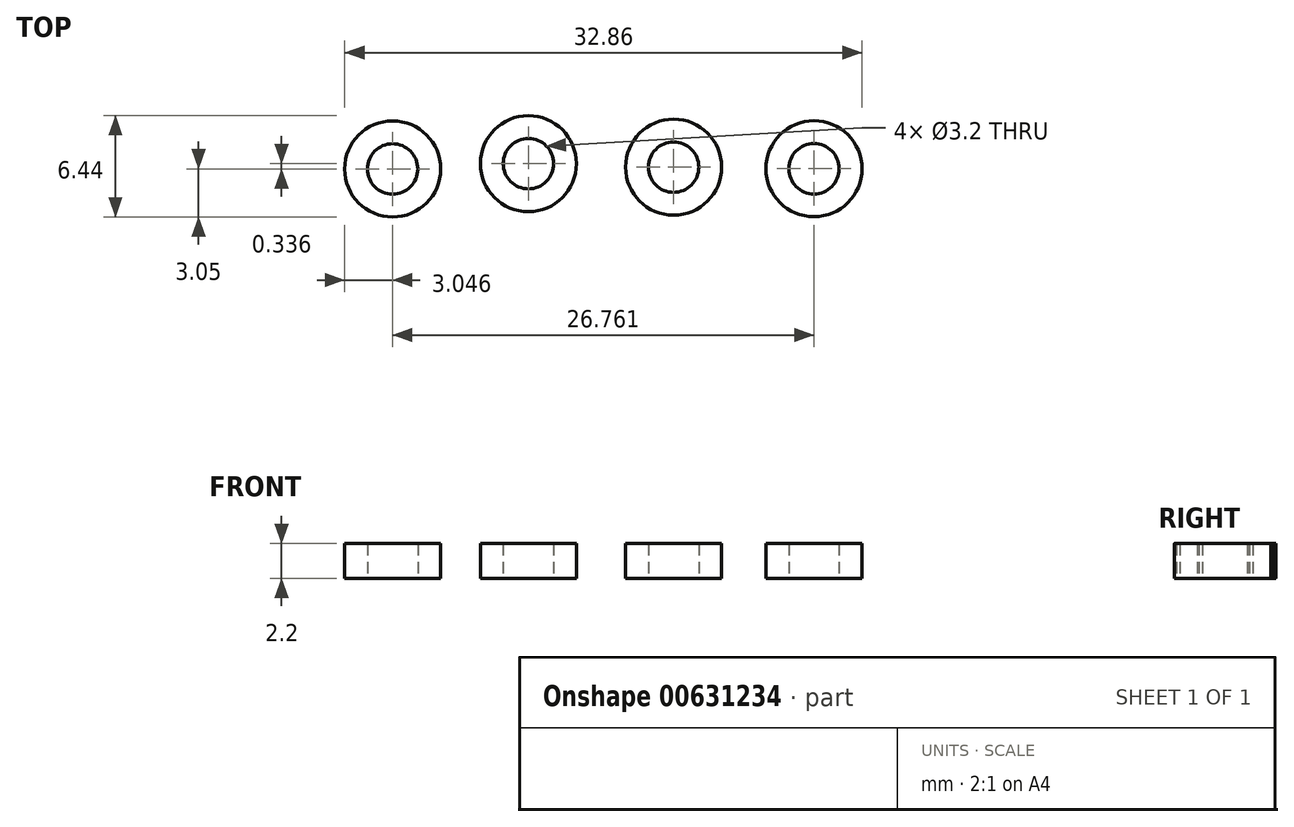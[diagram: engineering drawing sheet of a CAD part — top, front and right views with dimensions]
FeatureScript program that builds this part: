
annotation { "Feature Type Name" : "Feature", "Feature Type Description" : "" }
export const myFeature = defineFeature(function(context is Context, id is Id, definition is map)
    precondition{}
    {
        {
            var Q0;
            Q0=qCreatedBy(makeId("Top.planeOp"),FACE);
            var sketch = newSketch(context, id + "F0", { "sketchPlane" : qUnion([Q0])});
            skCircle(sketch, "E0", {"center": v(-7.28, -0.1) * mm, "radius": 3.05 * mm});
            skCircle(sketch, "E1", {"center": v(-7.28, -0.1) * mm, "radius": 1.6 * mm});
            skCircle(sketch, "E2", {"center": v(1.34, 0.25) * mm, "radius": 3.05 * mm});
            skCircle(sketch, "E3", {"center": v(1.34, 0.25) * mm, "radius": 1.6 * mm});
            skCircle(sketch, "E4", {"center": v(10.56, 0.02) * mm, "radius": 3.05 * mm});
            skCircle(sketch, "E5", {"center": v(10.56, 0.02) * mm, "radius": 1.6 * mm});
            skCircle(sketch, "E6", {"center": v(19.48, -0.08) * mm, "radius": 3.05 * mm});
            skCircle(sketch, "E7", {"center": v(19.48, -0.08) * mm, "radius": 1.6 * mm});
            skSolve(sketch);
        }
        {
            var Q0;
            Q0=makeQuery(id+"F0.imprint","IMPRINT",FACE,{"disambiguationData":[TD([[makeQuery(id+"F0.imprint","IMPRINT",EDGE,{"derivedFrom":sQuery(id+"F0.wireOp",EDGE,"E0")}),1.0]])]});
            var Q1;
            Q1=makeQuery(id+"F0.imprint","IMPRINT",FACE,{"disambiguationData":[TD([[makeQuery(id+"F0.imprint","IMPRINT",EDGE,{"derivedFrom":sQuery(id+"F0.wireOp",EDGE,"E2")}),1.0]])]});
            var Q2;
            Q2=makeQuery(id+"F0.imprint","IMPRINT",FACE,{"disambiguationData":[TD([[makeQuery(id+"F0.imprint","IMPRINT",EDGE,{"derivedFrom":sQuery(id+"F0.wireOp",EDGE,"E4")}),1.0]])]});
            var Q3;
            Q3=makeQuery(id+"F0.imprint","IMPRINT",FACE,{"disambiguationData":[TD([[makeQuery(id+"F0.imprint","IMPRINT",EDGE,{"derivedFrom":sQuery(id+"F0.wireOp",EDGE,"E6")}),1.0]])]});
            extrude(context, id + "F1", {"entities" : qUnion([Q0, Q1, Q2, Q3]), "depth" : 2.2 * mm, "offsetDistance" : 25 * mm});
        }
    });
